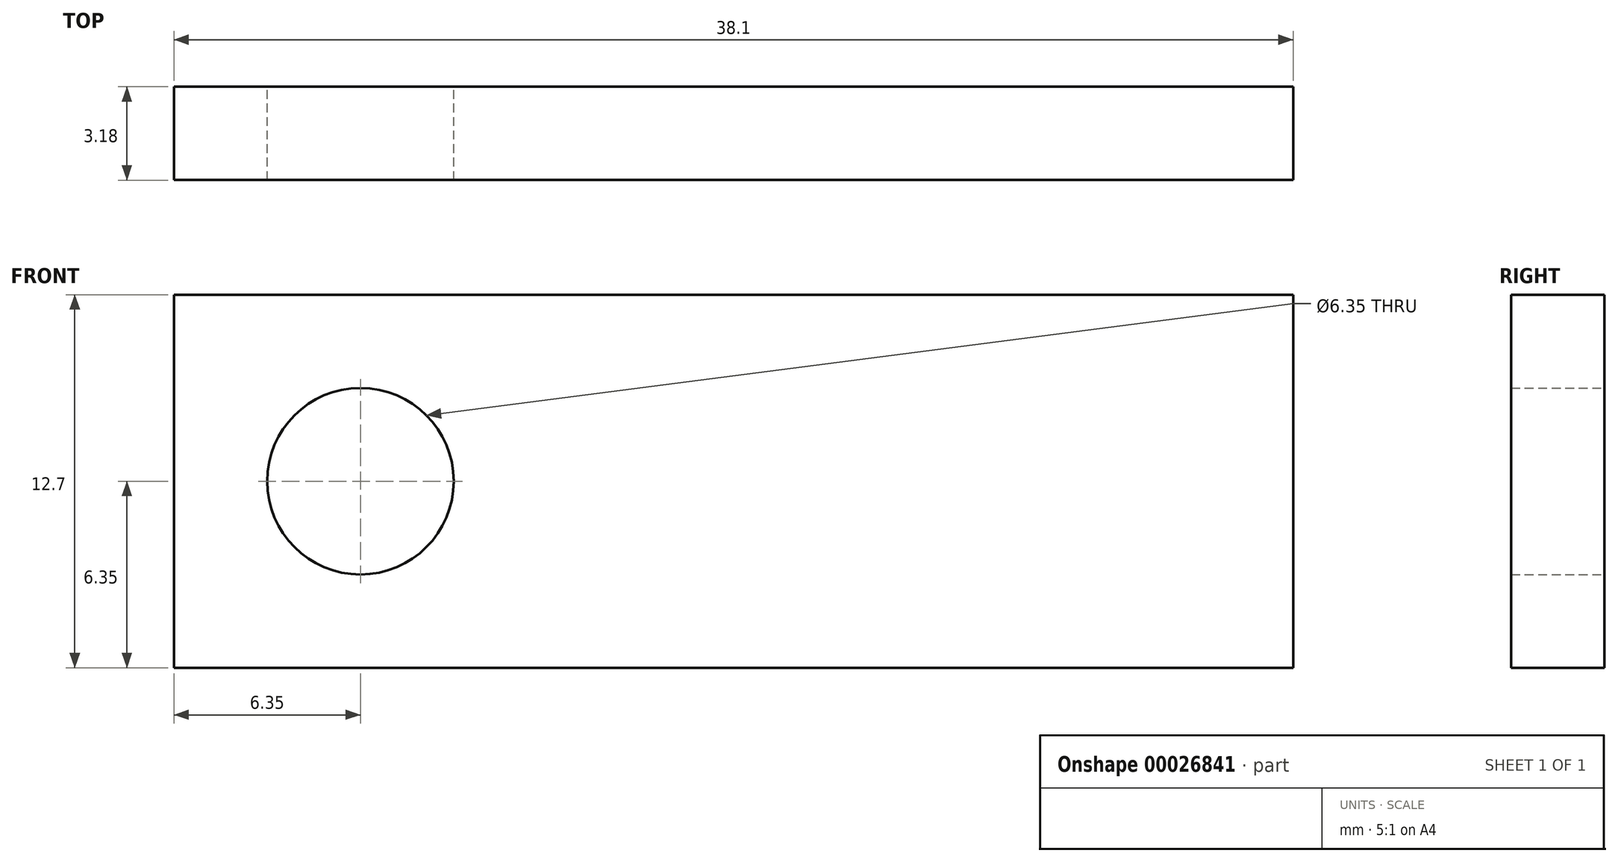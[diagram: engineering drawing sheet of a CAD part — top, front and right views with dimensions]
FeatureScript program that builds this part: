
annotation { "Feature Type Name" : "Feature", "Feature Type Description" : "" }
export const myFeature = defineFeature(function(context is Context, id is Id, definition is map)
    precondition{}
    {
        {
            var Q0;
            Q0=qCreatedBy(makeId("Front.planeOp"),FACE);
            var sketch = newSketch(context, id + "F0", { "sketchPlane" : qUnion([Q0])});
            skLineSegment(sketch, "E0.bottom", {"start": v(0, 0) * mm, "end": v(38.1, 0) * mm});
            skLineSegment(sketch, "E0.top", {"start": v(0, 12.7) * mm, "end": v(38.1, 12.7) * mm});
            skLineSegment(sketch, "E0.left", {"start": v(0, 0) * mm, "end": v(0, 12.7) * mm});
            skLineSegment(sketch, "E0.right", {"start": v(38.1, 0) * mm, "end": v(38.1, 12.7) * mm});
            skPoint(sketch, "E1", {"position": v(0, 6.35) * mm});
            skPoint(sketch, "E2", {"position": v(6.35, 6.35) * mm});
            skCircle(sketch, "E3", {"center": v(6.35, 6.35) * mm, "radius": 3.18 * mm});
            skSolve(sketch);
        }
        {
            var Q0;
            Q0=makeQuery(id+"F0.imprint","IMPRINT",FACE,{"disambiguationData":[TD([[makeQuery(id+"F0.imprint","IMPRINT",EDGE,{"derivedFrom":sQuery(id+"F0.wireOp",EDGE,"E0.bottom")}),1.0]])]});
            extrude(context, id + "F1", {"entities" : qUnion([Q0]), "depth" : 3.17 * mm});
        }
    });
